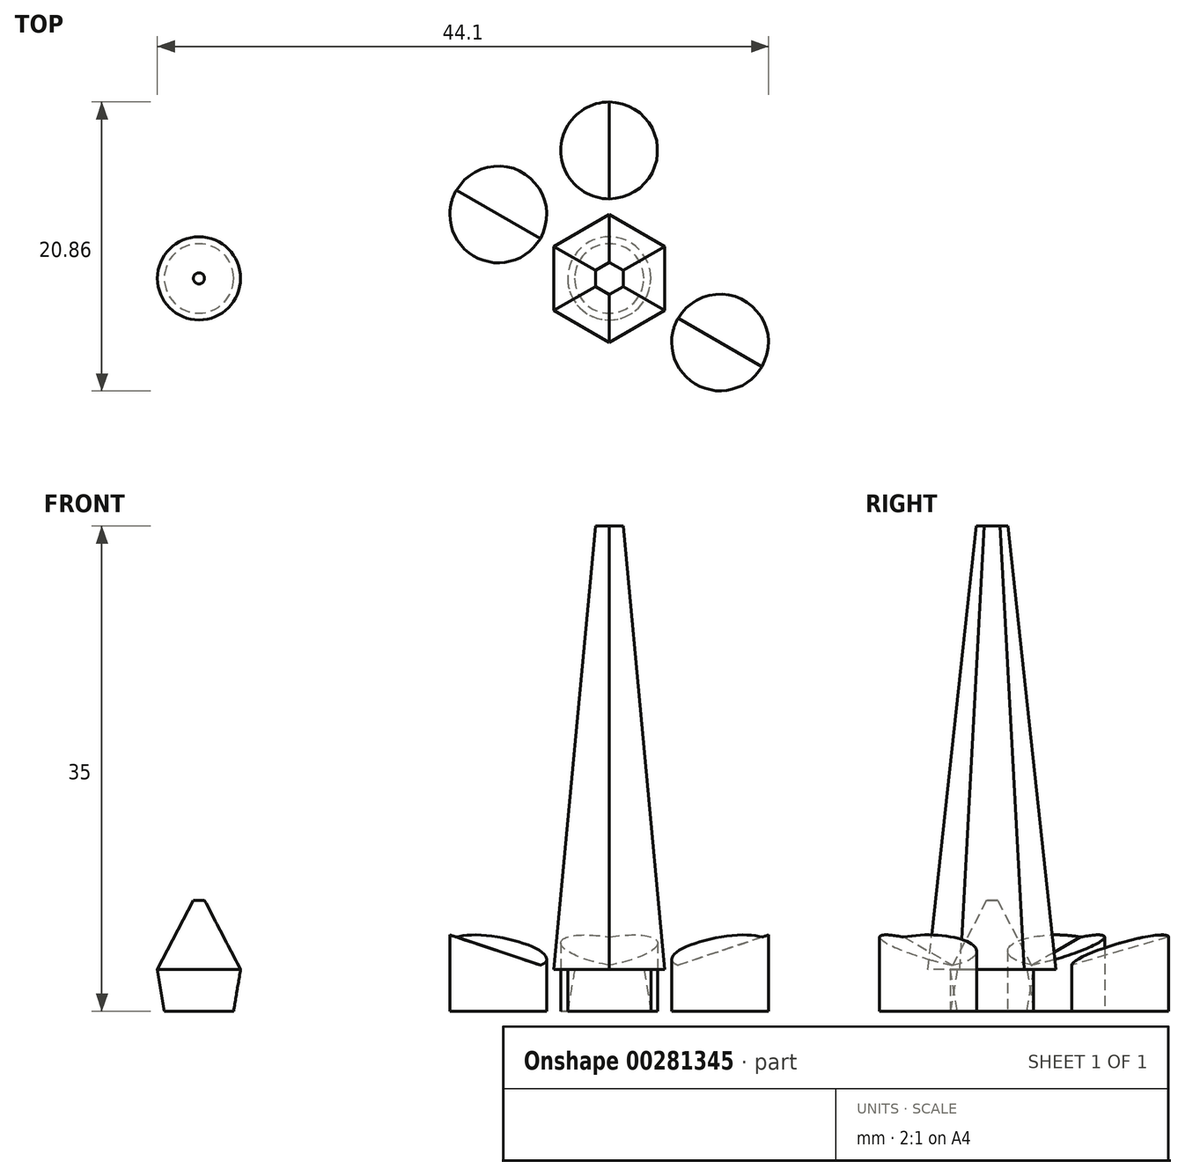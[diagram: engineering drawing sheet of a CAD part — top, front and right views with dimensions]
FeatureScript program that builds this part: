
annotation { "Feature Type Name" : "Feature", "Feature Type Description" : "" }
export const myFeature = defineFeature(function(context is Context, id is Id, definition is map)
    precondition{}
    {
        {
            var Q0;
            Q0=qCreatedBy(makeId("Top.planeOp"),FACE);
            var sketch = newSketch(context, id + "F0", { "sketchPlane" : qUnion([Q0])});
            skCircle(sketch, "E0.cCircle", {"center": v(0, 0) * mm, "radius": 16 * mm, "construction": true});
            skLineSegment(sketch, "E0.0", {"start": v(16, 9.24) * mm, "end": v(16, -9.24) * mm});
            skLineSegment(sketch, "E0.1", {"start": v(16, -9.24) * mm, "end": v(0, -18.48) * mm});
            skLineSegment(sketch, "E0.2", {"start": v(0, -18.48) * mm, "end": v(-16, -9.24) * mm});
            skLineSegment(sketch, "E0.3", {"start": v(-16, -9.24) * mm, "end": v(-16, 9.24) * mm});
            skLineSegment(sketch, "E0.4", {"start": v(-16, 9.24) * mm, "end": v(0, 18.48) * mm});
            skLineSegment(sketch, "E0.5", {"start": v(0, 18.48) * mm, "end": v(16, 9.24) * mm});
            skPoint(sketch, "E0.0.midPoint", {"position": v(16, 0) * mm});
            skSolve(sketch);
        }
        {
            var Q0;
            Q0=makeQuery(id+"F0.imprint","IMPRINT",FACE,{"disambiguationData":[TD([[makeQuery(id+"F0.imprint","IMPRINT",EDGE,{"derivedFrom":sQuery(id+"F0.wireOp",EDGE,"E0.0")}),-1.0]])]});
            extrude(context, id + "F1", {"entities" : qUnion([Q0]), "depth" : 7 * mm});
        }
        {
            var Q0;
            Q0=makeQuery(id+"F1.opExtrude","CAP_FACE",FACE,{"disambiguationData":[OSD([sQuery(id+"F0.wireOp",EDGE,"E0.0"),sQuery(id+"F0.wireOp",EDGE,"E0.1"),sQuery(id+"F0.wireOp",EDGE,"E0.2"),sQuery(id+"F0.wireOp",EDGE,"E0.3"),sQuery(id+"F0.wireOp",EDGE,"E0.4"),sQuery(id+"F0.wireOp",EDGE,"E0.5")])],"isStart":false});
            cPlane(context, id + "F2", {"entities" : qUnion([Q0]), "cplaneType" : CPlaneType.OFFSET, "offset" : 4 * mm, "oppositeDirection" : true, "width" : 150 * mm, "height" : 150 * mm});
        }
        {
            var Q0;
            Q0=qCreatedBy(id+"F2.planeOp",FACE);
            var sketch = newSketch(context, id + "F3", { "sketchPlane" : qUnion([Q0])});
            skCircle(sketch, "E1.cCircle", {"center": v(0, 0) * mm, "radius": 4 * mm, "construction": true});
            skLineSegment(sketch, "E1.0", {"start": v(4, 2.3) * mm, "end": v(4, -2.3) * mm});
            skLineSegment(sketch, "E1.1", {"start": v(4, -2.3) * mm, "end": v(0, -4.62) * mm});
            skLineSegment(sketch, "E1.2", {"start": v(0, -4.62) * mm, "end": v(-4, -2.3) * mm});
            skLineSegment(sketch, "E1.3", {"start": v(-4, -2.3) * mm, "end": v(-4, 2.3) * mm});
            skLineSegment(sketch, "E1.4", {"start": v(-4, 2.3) * mm, "end": v(0, 4.62) * mm});
            skLineSegment(sketch, "E1.5", {"start": v(0, 4.62) * mm, "end": v(4, 2.3) * mm});
            skPoint(sketch, "E1.0.midPoint", {"position": v(4, 0) * mm});
            skSolve(sketch);
        }
        {
            var Q1;
            Q1=makeQuery(id+"F1.opExtrude","CAP_FACE",FACE,{"disambiguationData":[OSD([sQuery(id+"F0.wireOp",EDGE,"E0.0"),sQuery(id+"F0.wireOp",EDGE,"E0.1"),sQuery(id+"F0.wireOp",EDGE,"E0.2"),sQuery(id+"F0.wireOp",EDGE,"E0.3"),sQuery(id+"F0.wireOp",EDGE,"E0.4"),sQuery(id+"F0.wireOp",EDGE,"E0.5")])],"isStart":false});
            var Q2;
            Q2 = qSketchRegion(id + "F3", true);
            loft(context, id + "F4", {"operationType" : NewBodyOperationType.REMOVE, "sheetProfilesArray" : [{ "sheetProfileEntities" : qUnion([Q1]) }, { "sheetProfileEntities" : qUnion([Q2]) }]});
        }
        {
            var Q0;
            Q0=makeQuery(id+"F1.opExtrude","CAP_FACE",FACE,{"disambiguationData":[OSD([sQuery(id+"F0.wireOp",EDGE,"E0.0"),sQuery(id+"F0.wireOp",EDGE,"E0.1"),sQuery(id+"F0.wireOp",EDGE,"E0.2"),sQuery(id+"F0.wireOp",EDGE,"E0.3"),sQuery(id+"F0.wireOp",EDGE,"E0.4"),sQuery(id+"F0.wireOp",EDGE,"E0.5")])],"isStart":true});
            var sketch = newSketch(context, id + "F5", { "sketchPlane" : qUnion([Q0])});
            skCircle(sketch, "E2", {"center": v(0, 0) * mm, "radius": 3 * mm});
            skSolve(sketch);
        }
        {
            var Q0;
            Q0=qCreatedBy(id+"F2.planeOp",FACE);
            var sketch = newSketch(context, id + "F6", { "sketchPlane" : qUnion([Q0])});
            skCircle(sketch, "E3", {"center": v(0, 0) * mm, "radius": 2.5 * mm});
            skSolve(sketch);
        }
        {
            var Q1;
            Q1=makeQuery(id+"F5.imprint","IMPRINT",FACE,{"disambiguationData":[TD([[makeQuery(id+"F5.imprint","IMPRINT",EDGE,{"derivedFrom":sQuery(id+"F5.wireOp",EDGE,"E2")}),1.0]])]});
            var Q2;
            Q2=makeQuery(id+"F6.imprint","IMPRINT",FACE,{"disambiguationData":[TD([[makeQuery(id+"F6.imprint","IMPRINT",EDGE,{"derivedFrom":sQuery(id+"F6.wireOp",EDGE,"E3")}),1.0]])]});
            loft(context, id + "F7", {"operationType" : NewBodyOperationType.REMOVE, "sheetProfilesArray" : [{ "sheetProfileEntities" : qUnion([Q1]) }, { "sheetProfileEntities" : qUnion([Q2]) }]});
        }
        {
            var Q0;
            Q0=makeQuery(id+"F1.opExtrude","CAP_FACE",FACE,{"disambiguationData":[OSD([sQuery(id+"F0.wireOp",EDGE,"E0.0"),sQuery(id+"F0.wireOp",EDGE,"E0.1"),sQuery(id+"F0.wireOp",EDGE,"E0.2"),sQuery(id+"F0.wireOp",EDGE,"E0.3"),sQuery(id+"F0.wireOp",EDGE,"E0.4"),sQuery(id+"F0.wireOp",EDGE,"E0.5")])],"isStart":true});
            var sketch = newSketch(context, id + "F8", { "sketchPlane" : qUnion([Q0])});
            skCircle(sketch, "E4", {"center": v(-8, 4.62) * mm, "radius": 3.5 * mm});
            skCircle(sketch, "E5", {"center": v(0, 9.24) * mm, "radius": 3.5 * mm});
            skCircle(sketch, "E6.MirrorC", {"center": v(8, 4.62) * mm, "radius": 3.5 * mm});
            skCircle(sketch, "E7.MirrorC", {"center": v(-8, -4.62) * mm, "radius": 3.5 * mm});
            skCircle(sketch, "E8.MirrorC", {"center": v(0, -9.24) * mm, "radius": 3.5 * mm});
            skCircle(sketch, "E9.MirrorC", {"center": v(8, -4.62) * mm, "radius": 3.5 * mm});
            skSolve(sketch);
        }
        {
            var Q0;
            Q0=makeQuery(id+"F8.imprint","IMPRINT",FACE,{"disambiguationData":[TD([[makeQuery(id+"F8.imprint","IMPRINT",EDGE,{"derivedFrom":sQuery(id+"F8.wireOp",EDGE,"E4")}),1.0]])]});
            var Q1;
            Q1=makeQuery(id+"F8.imprint","IMPRINT",FACE,{"disambiguationData":[TD([[makeQuery(id+"F8.imprint","IMPRINT",EDGE,{"derivedFrom":sQuery(id+"F8.wireOp",EDGE,"E5")}),1.0]])]});
            var Q2;
            Q2=makeQuery(id+"F8.imprint","IMPRINT",FACE,{"disambiguationData":[TD([[makeQuery(id+"F8.imprint","IMPRINT",EDGE,{"derivedFrom":sQuery(id+"F8.wireOp",EDGE,"E6.MirrorC")}),-1.0]])]});
            var Q3;
            Q3=makeQuery(id+"F8.imprint","IMPRINT",FACE,{"disambiguationData":[TD([[makeQuery(id+"F8.imprint","IMPRINT",EDGE,{"derivedFrom":sQuery(id+"F8.wireOp",EDGE,"E9.MirrorC")}),1.0]])]});
            var Q4;
            Q4=makeQuery(id+"F8.imprint","IMPRINT",FACE,{"disambiguationData":[TD([[makeQuery(id+"F8.imprint","IMPRINT",EDGE,{"derivedFrom":sQuery(id+"F8.wireOp",EDGE,"E8.MirrorC")}),-1.0]])]});
            var Q5;
            Q5=makeQuery(id+"F8.imprint","IMPRINT",FACE,{"disambiguationData":[TD([[makeQuery(id+"F8.imprint","IMPRINT",EDGE,{"derivedFrom":sQuery(id+"F8.wireOp",EDGE,"E7.MirrorC")}),-1.0]])]});
            extrude(context, id + "F9", {"entities" : qUnion([Q0, Q1, Q2, Q3, Q4, Q5]), "operationType" : NewBodyOperationType.REMOVE, "oppositeDirection" : true, "depth" : 7 * mm});
        }
        {
            var Q0;
            Q0=makeQuery(id+"F4.boolean.opBoolean","COPY",FACE,{"derivedFrom":makeQuery(id+"F4.opLoft","CAP_FACE",FACE,{"disambiguationData":[OSD([makeQuery(id+"F3.imprint","IMPRINT",FACE,{"disambiguationData":[TD([[makeQuery(id+"F3.imprint","IMPRINT",EDGE,{"derivedFrom":sQuery(id+"F3.wireOp",EDGE,"E1.0")}),-1.0]])]})])],"isStart":true})});
            cPlane(context, id + "F10", {"entities" : qUnion([Q0]), "cplaneType" : CPlaneType.OFFSET, "offset" : 32 * mm, "width" : 150 * mm, "height" : 150 * mm});
        }
        {
            var Q0;
            Q0=qCreatedBy(id+"F10.planeOp",FACE);
            var sketch = newSketch(context, id + "F11", { "sketchPlane" : qUnion([Q0])});
            skCircle(sketch, "E10.cCircle", {"center": v(0, 0) * mm, "radius": 1 * mm, "construction": true});
            skLineSegment(sketch, "E10.0", {"start": v(1, 0.58) * mm, "end": v(1, -0.58) * mm});
            skLineSegment(sketch, "E10.1", {"start": v(1, -0.58) * mm, "end": v(0, -1.15) * mm});
            skLineSegment(sketch, "E10.2", {"start": v(0, -1.15) * mm, "end": v(-1, -0.58) * mm});
            skLineSegment(sketch, "E10.3", {"start": v(-1, -0.58) * mm, "end": v(-1, 0.58) * mm});
            skLineSegment(sketch, "E10.4", {"start": v(-1, 0.58) * mm, "end": v(0, 1.15) * mm});
            skLineSegment(sketch, "E10.5", {"start": v(0, 1.15) * mm, "end": v(1, 0.58) * mm});
            skPoint(sketch, "E10.0.midPoint", {"position": v(1, 0) * mm});
            skSolve(sketch);
        }
        {
            var Q0;
            Q0=makeQuery(id+"F4.boolean.opBoolean","COPY",FACE,{"derivedFrom":makeQuery(id+"F4.opLoft","CAP_FACE",FACE,{"disambiguationData":[OSD([makeQuery(id+"F3.imprint","IMPRINT",FACE,{"disambiguationData":[TD([[makeQuery(id+"F3.imprint","IMPRINT",EDGE,{"derivedFrom":sQuery(id+"F3.wireOp",EDGE,"E1.0")}),-1.0]])]})])],"isStart":true})});
            var sketch = newSketch(context, id + "F12", { "sketchPlane" : qUnion([Q0])});
            skCircle(sketch, "E11.cCircle", {"center": v(0, 0) * mm, "radius": 4 * mm, "construction": true});
            skLineSegment(sketch, "E11.0", {"start": v(4, 2.3) * mm, "end": v(4, -2.3) * mm});
            skLineSegment(sketch, "E11.1", {"start": v(4, -2.3) * mm, "end": v(0, -4.62) * mm});
            skLineSegment(sketch, "E11.2", {"start": v(0, -4.62) * mm, "end": v(-4, -2.3) * mm});
            skLineSegment(sketch, "E11.3", {"start": v(-4, -2.3) * mm, "end": v(-4, 2.3) * mm});
            skLineSegment(sketch, "E11.4", {"start": v(-4, 2.3) * mm, "end": v(0, 4.62) * mm});
            skLineSegment(sketch, "E11.5", {"start": v(0, 4.62) * mm, "end": v(4, 2.3) * mm});
            skPoint(sketch, "E11.0.midPoint", {"position": v(4, 0) * mm});
            skSolve(sketch);
        }
        {
            var Q1;
            Q1 = qSketchRegion(id + "F12", true);
            var Q2;
            Q2 = qSketchRegion(id + "F11", true);
            loft(context, id + "F13", {"operationType" : NewBodyOperationType.ADD, "sheetProfilesArray" : [{ "sheetProfileEntities" : qUnion([Q1]) }, { "sheetProfileEntities" : qUnion([Q2]) }]});
        }
        {
            var Q0;
            Q0=qCreatedBy(makeId("Top.planeOp"),FACE);
            var sketch = newSketch(context, id + "F14", { "sketchPlane" : qUnion([Q0])});
            skCircle(sketch, "E12", {"center": v(-29.6, 0) * mm, "radius": 2.5 * mm});
            skSolve(sketch);
        }
        {
            var Q0;
            Q0=makeQuery(id+"F14.imprint","IMPRINT",FACE,{"disambiguationData":[TD([[makeQuery(id+"F14.imprint","IMPRINT",EDGE,{"derivedFrom":sQuery(id+"F14.wireOp",EDGE,"E12")}),1.0]])]});
            cPlane(context, id + "F15", {"entities" : qUnion([Q0]), "cplaneType" : CPlaneType.OFFSET, "offset" : 3 * mm, "width" : 150 * mm, "height" : 150 * mm});
        }
        {
            var Q0;
            Q0=qCreatedBy(id+"F15.planeOp",FACE);
            var sketch = newSketch(context, id + "F16", { "sketchPlane" : qUnion([Q0])});
            skCircle(sketch, "E13", {"center": v(-29.6, 0) * mm, "radius": 3 * mm});
            skSolve(sketch);
        }
        {
            var Q0;
            Q0=qCreatedBy(id+"F15.planeOp",FACE);
            cPlane(context, id + "F17", {"entities" : qUnion([Q0]), "cplaneType" : CPlaneType.OFFSET, "offset" : 5 * mm, "width" : 150 * mm, "height" : 150 * mm});
        }
        {
            var Q0;
            Q0=qCreatedBy(id+"F17.planeOp",FACE);
            var sketch = newSketch(context, id + "F18", { "sketchPlane" : qUnion([Q0])});
            skCircle(sketch, "E14", {"center": v(-29.6, 0) * mm, "radius": 0.4 * mm});
            skSolve(sketch);
        }
        {
            var Q0;
            Q0=makeQuery(id+"F14.imprint","IMPRINT",FACE,{"disambiguationData":[TD([[makeQuery(id+"F14.imprint","IMPRINT",EDGE,{"derivedFrom":sQuery(id+"F14.wireOp",EDGE,"E12")}),1.0]])]});
            var Q1;
            Q1=makeQuery(id+"F16.imprint","IMPRINT",FACE,{"disambiguationData":[TD([[makeQuery(id+"F16.imprint","IMPRINT",EDGE,{"derivedFrom":sQuery(id+"F16.wireOp",EDGE,"E13")}),1.0]])]});
            loft(context, id + "F19", {"sheetProfilesArray" : [{ "sheetProfileEntities" : qUnion([Q0]) }, { "sheetProfileEntities" : qUnion([Q1]) }]});
        }
        {
            var Q1;
            Q1=makeQuery(id+"F19.opLoft","CAP_FACE",FACE,{"disambiguationData":[OSD([makeQuery(id+"F16.imprint","IMPRINT",FACE,{"disambiguationData":[TD([[makeQuery(id+"F16.imprint","IMPRINT",EDGE,{"derivedFrom":sQuery(id+"F16.wireOp",EDGE,"E13")}),1.0]])]})])],"isStart":true});
            var Q2;
            Q2=makeQuery(id+"F18.imprint","IMPRINT",FACE,{"disambiguationData":[TD([[makeQuery(id+"F18.imprint","IMPRINT",EDGE,{"derivedFrom":sQuery(id+"F18.wireOp",EDGE,"E14")}),1.0]])]});
            loft(context, id + "F20", {"operationType" : NewBodyOperationType.ADD, "sheetProfilesArray" : [{ "sheetProfileEntities" : qUnion([Q1]) }, { "sheetProfileEntities" : qUnion([Q2]) }]});
        }
    });
